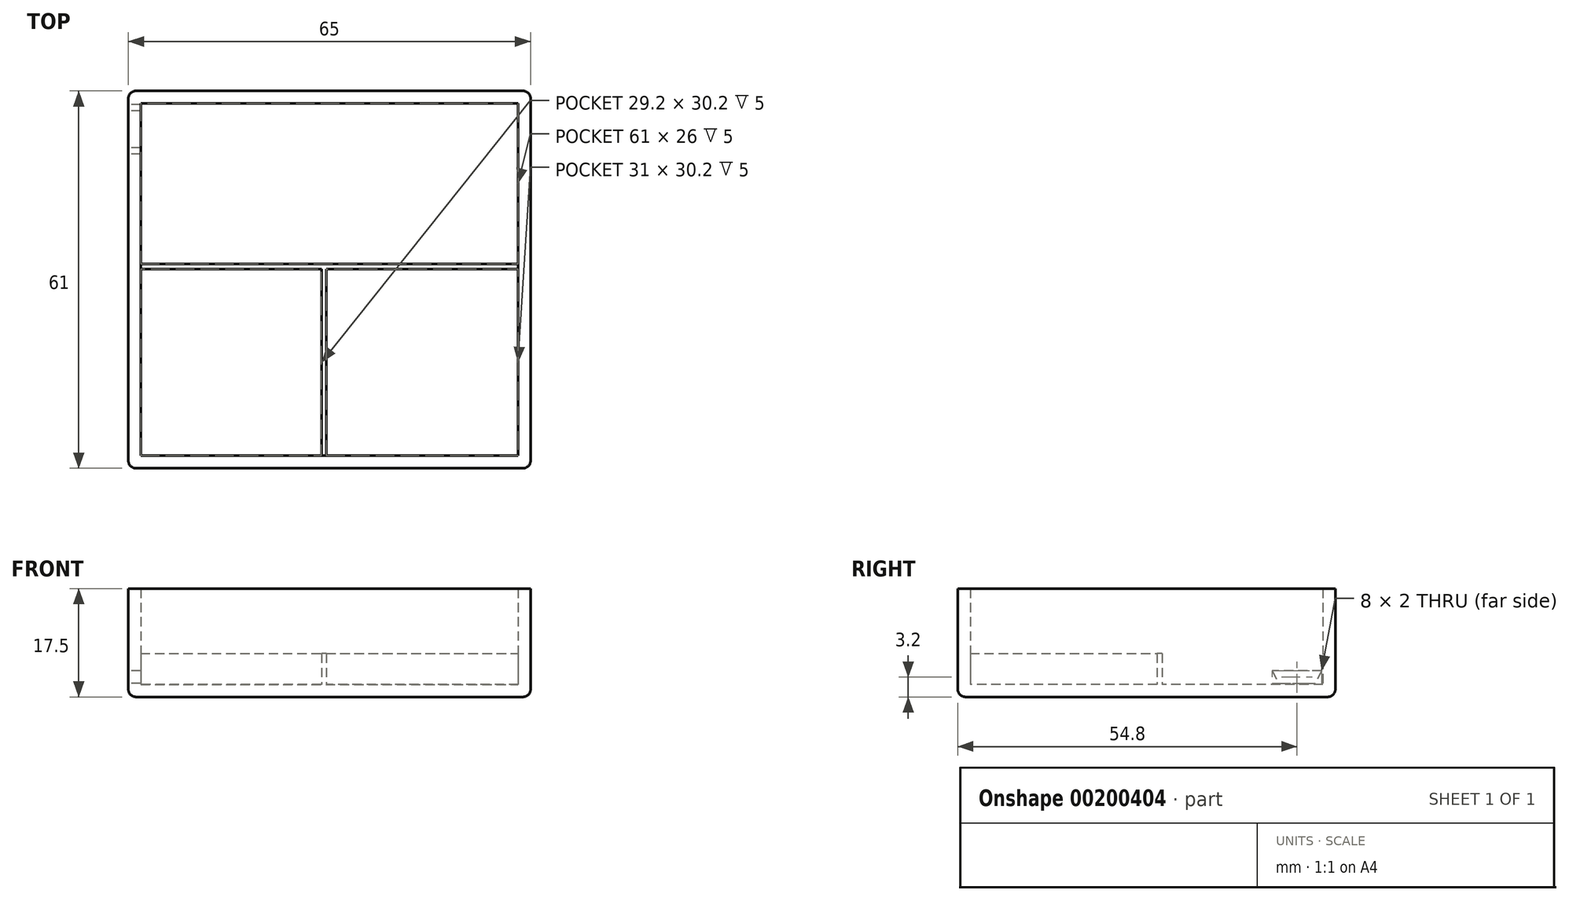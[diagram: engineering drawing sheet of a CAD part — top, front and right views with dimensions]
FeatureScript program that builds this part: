
annotation { "Feature Type Name" : "Feature", "Feature Type Description" : "" }
export const myFeature = defineFeature(function(context is Context, id is Id, definition is map)
    precondition{}
    {
        {
            var Q0;
            Q0=qCreatedBy(makeId("Top.planeOp"),FACE);
            var sketch = newSketch(context, id + "F0", { "sketchPlane" : qUnion([Q0])});
            skLineSegment(sketch, "E0.bottom", {"start": v(32.5, 30.5) * mm, "end": v(-32.5, 30.5) * mm});
            skLineSegment(sketch, "E0.top", {"start": v(32.5, -30.5) * mm, "end": v(-32.5, -30.5) * mm});
            skLineSegment(sketch, "E0.left", {"start": v(32.5, 30.5) * mm, "end": v(32.5, -30.5) * mm});
            skLineSegment(sketch, "E0.right", {"start": v(-32.5, 30.5) * mm, "end": v(-32.5, -30.5) * mm});
            skPoint(sketch, "E0.middle", {"position": v(0, 0) * mm});
            skSolve(sketch);
        }
        {
            var Q0;
            Q0=makeQuery(id+"F0.imprint","IMPRINT",FACE,{"disambiguationData":[TD([[makeQuery(id+"F0.imprint","IMPRINT",EDGE,{"derivedFrom":sQuery(id+"F0.wireOp",EDGE,"E0.bottom")}),1.0]])]});
            extrude(context, id + "F1", {"entities" : qUnion([Q0]), "depth" : 17.5 * mm});
        }
        {
            var Q0;
            Q0=makeQuery(id+"F1.opExtrude","CAP_FACE",FACE,{"disambiguationData":[OSD([sQuery(id+"F0.wireOp",EDGE,"E0.bottom"),sQuery(id+"F0.wireOp",EDGE,"E0.top"),sQuery(id+"F0.wireOp",EDGE,"E0.left"),sQuery(id+"F0.wireOp",EDGE,"E0.right")])],"isStart":false});
            shell(context, id + "F2", {"entities" : qUnion([Q0]), "thickness" : 2 * mm});
        }
        {
            var Q0;
            Q0=makeQuery(id+"F1.opExtrude","SWEPT_EDGE",EDGE,{"disambiguationData":[OSD([sQuery(id+"F0.wireOp",EDGE,"E0.top"),sQuery(id+"F0.wireOp",EDGE,"E0.left")])]});
            var Q1;
            Q1=makeQuery(id+"F1.opExtrude","SWEPT_EDGE",EDGE,{"disambiguationData":[OSD([sQuery(id+"F0.wireOp",EDGE,"E0.bottom"),sQuery(id+"F0.wireOp",EDGE,"E0.left")])]});
            var Q2;
            Q2=makeQuery(id+"F1.opExtrude","SWEPT_EDGE",EDGE,{"disambiguationData":[OSD([sQuery(id+"F0.wireOp",EDGE,"E0.bottom"),sQuery(id+"F0.wireOp",EDGE,"E0.right")])]});
            var Q3;
            Q3=makeQuery(id+"F1.opExtrude","SWEPT_EDGE",EDGE,{"disambiguationData":[OSD([sQuery(id+"F0.wireOp",EDGE,"E0.top"),sQuery(id+"F0.wireOp",EDGE,"E0.right")])]});
            var Q4;
            Q4=makeQuery(id+"F1.opExtrude","CAP_EDGE",EDGE,{"disambiguationData":[OSD([sQuery(id+"F0.wireOp",EDGE,"E0.top")])],"isStart":true});
            var Q5;
            Q5=makeQuery(id+"F1.opExtrude","CAP_EDGE",EDGE,{"disambiguationData":[OSD([sQuery(id+"F0.wireOp",EDGE,"E0.right")])],"isStart":true});
            var Q6;
            Q6=makeQuery(id+"F1.opExtrude","CAP_EDGE",EDGE,{"disambiguationData":[OSD([sQuery(id+"F0.wireOp",EDGE,"E0.left")])],"isStart":true});
            var Q7;
            Q7=makeQuery(id+"F1.opExtrude","CAP_EDGE",EDGE,{"disambiguationData":[OSD([sQuery(id+"F0.wireOp",EDGE,"E0.bottom")])],"isStart":true});
            var Q8;
            Q8=makeQuery(id+"F1.opExtrude","CAP_FACE",FACE,{"disambiguationData":[OSD([sQuery(id+"F0.wireOp",EDGE,"E0.bottom"),sQuery(id+"F0.wireOp",EDGE,"E0.top"),sQuery(id+"F0.wireOp",EDGE,"E0.left"),sQuery(id+"F0.wireOp",EDGE,"E0.right")])],"isStart":true});
            fillet(context, id + "F3", {"entities" : qUnion([Q0, Q1, Q2, Q3, Q4, Q5, Q6, Q7, Q8]), "radius" : 1.2 * mm, "tangentPropagation" : true, "allowEdgeOverflow" : false});
        }
        {
            var Q0;
            Q0=makeQuery(id+"F2.opShell","OFFSET_FACE",FACE,{"disambiguationData":[OSD([sQuery(id+"F0.wireOp",EDGE,"E0.bottom"),sQuery(id+"F0.wireOp",EDGE,"E0.top"),sQuery(id+"F0.wireOp",EDGE,"E0.left"),sQuery(id+"F0.wireOp",EDGE,"E0.right")])]});
            var sketch = newSketch(context, id + "F4", { "sketchPlane" : qUnion([Q0])});
            skLineSegment(sketch, "E1.bottom", {"start": v(-30.5, 2.5) * mm, "end": v(30.5, 2.5) * mm});
            skLineSegment(sketch, "E1.top", {"start": v(-30.5, 1.7) * mm, "end": v(30.5, 1.7) * mm});
            skLineSegment(sketch, "E1.left", {"start": v(-30.5, 2.5) * mm, "end": v(-30.5, 1.7) * mm});
            skLineSegment(sketch, "E1.right", {"start": v(30.5, 2.5) * mm, "end": v(30.5, 1.7) * mm});
            skLineSegment(sketch, "E2.bottom", {"start": v(-0.5, -28.5) * mm, "end": v(-1.3, -28.5) * mm});
            skLineSegment(sketch, "E2.top", {"start": v(-0.5, 1.7) * mm, "end": v(-1.3, 1.7) * mm});
            skLineSegment(sketch, "E2.left", {"start": v(-0.5, -28.5) * mm, "end": v(-0.5, 1.7) * mm});
            skLineSegment(sketch, "E2.right", {"start": v(-1.3, -28.5) * mm, "end": v(-1.3, 1.7) * mm});
            skSolve(sketch);
        }
        {
            var Q0;
            Q0 = qSketchRegion(id + "F4", true);
            extrude(context, id + "F5", {"entities" : qUnion([Q0]), "operationType" : NewBodyOperationType.ADD, "depth" : 5 * mm});
        }
        {
            var Q0;
            Q0=makeQuery(id+"F1.opExtrude","SWEPT_FACE",FACE,{"disambiguationData":[OSD([sQuery(id+"F0.wireOp",EDGE,"E0.right")])]});
            var sketch = newSketch(context, id + "F6", { "sketchPlane" : qUnion([Q0])});
            skLineSegment(sketch, "E3", {"start": v(-28.3, 4.2) * mm, "end": v(-20.3, 4.2) * mm});
            skLineSegment(sketch, "E4", {"start": v(-21.3, 2.2) * mm, "end": v(-27.3, 2.2) * mm});
            skLineSegment(sketch, "E5", {"start": v(-20.3, 4.2) * mm, "end": v(-21.3, 2.2) * mm});
            skLineSegment(sketch, "E6", {"start": v(-28.3, 4.2) * mm, "end": v(-27.3, 2.2) * mm});
            skSolve(sketch);
        }
        {
            var Q0;
            Q0=makeQuery(id+"F6.imprint","IMPRINT",FACE,{"disambiguationData":[TD([[makeQuery(id+"F6.imprint","IMPRINT",EDGE,{"derivedFrom":sQuery(id+"F6.wireOp",EDGE,"E3")}),-1.0]])]});
            var Q1;
            Q1=makeQuery(id+"F2.opShell","OFFSET_FACE",FACE,{"disambiguationData":[OSD([sQuery(id+"F0.wireOp",EDGE,"E0.right")])]});
            extrude(context, id + "F7", {"entities" : qUnion([Q0]), "operationType" : NewBodyOperationType.REMOVE, "endBound" : BoundingType.UP_TO_SURFACE, "oppositeDirection" : true, "endBoundEntityFace" : qUnion([Q1]), "depth" : 25 * mm});
        }
    });
